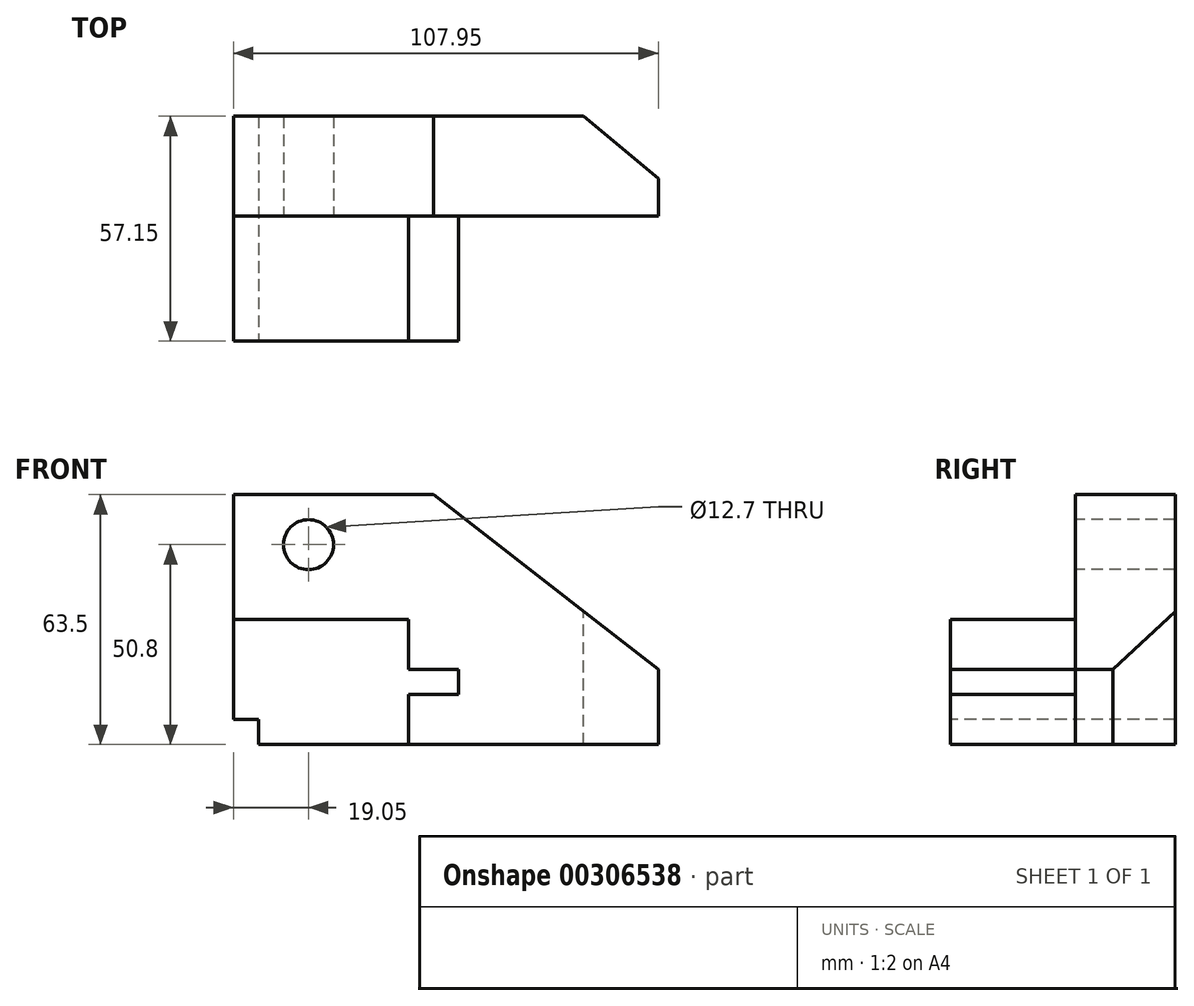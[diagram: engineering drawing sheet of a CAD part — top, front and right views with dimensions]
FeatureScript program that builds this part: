
annotation { "Feature Type Name" : "Feature", "Feature Type Description" : "" }
export const myFeature = defineFeature(function(context is Context, id is Id, definition is map)
    precondition{}
    {
        {
            var Q0;
            Q0=qCreatedBy(makeId("Front.planeOp"),FACE);
            var sketch = newSketch(context, id + "F0", { "sketchPlane" : qUnion([Q0])});
            skLineSegment(sketch, "E0", {"start": v(0, 0) * mm, "end": v(0, 63.5) * mm});
            skLineSegment(sketch, "E1", {"start": v(0, 63.5) * mm, "end": v(107.95, 63.5) * mm});
            skLineSegment(sketch, "E2", {"start": v(107.95, 63.5) * mm, "end": v(107.95, 0) * mm});
            skLineSegment(sketch, "E3", {"start": v(107.95, 0) * mm, "end": v(0, 0) * mm});
            skSolve(sketch);
        }
        {
            var Q0;
            Q0 = qSketchRegion(id + "F0", true);
            extrude(context, id + "F1", {"entities" : qUnion([Q0]), "depth" : 57.15 * mm});
        }
        {
            var Q0;
            Q0=makeQuery(id+"F1.opExtrude","SWEPT_FACE",FACE,{"disambiguationData":[OSD([sQuery(id+"F0.wireOp",EDGE,"E1")])]});
            var sketch = newSketch(context, id + "F2", { "sketchPlane" : qUnion([Q0])});
            skLineSegment(sketch, "E4", {"start": v(0, -57.15) * mm, "end": v(0, -25.4) * mm});
            skLineSegment(sketch, "E5", {"start": v(0, -25.4) * mm, "end": v(107.95, -25.4) * mm});
            skLineSegment(sketch, "E6", {"start": v(107.95, -25.4) * mm, "end": v(107.95, -57.15) * mm});
            skLineSegment(sketch, "E7", {"start": v(107.95, -57.15) * mm, "end": v(0, -57.15) * mm});
            skSolve(sketch);
        }
        {
            var Q0;
            Q0 = qSketchRegion(id + "F2", true);
            extrude(context, id + "F3", {"entities" : qUnion([Q0]), "operationType" : NewBodyOperationType.REMOVE, "oppositeDirection" : true, "depth" : 31.75 * mm});
        }
        {
            var Q0;
            Q0=makeQuery(id+"F1.opExtrude","CAP_FACE",FACE,{"disambiguationData":[OSD([sQuery(id+"F0.wireOp",EDGE,"E0"),sQuery(id+"F0.wireOp",EDGE,"E1"),sQuery(id+"F0.wireOp",EDGE,"E2"),sQuery(id+"F0.wireOp",EDGE,"E3")])],"isStart":false});
            var sketch = newSketch(context, id + "F4", { "sketchPlane" : qUnion([Q0])});
            skLineSegment(sketch, "E8", {"start": v(0, 31.75) * mm, "end": v(44.45, 31.75) * mm});
            skLineSegment(sketch, "E9", {"start": v(44.45, 31.75) * mm, "end": v(44.45, 19.05) * mm});
            skLineSegment(sketch, "E10", {"start": v(44.45, 19.05) * mm, "end": v(57.15, 19.05) * mm});
            skLineSegment(sketch, "E11", {"start": v(57.15, 19.05) * mm, "end": v(57.15, 12.7) * mm});
            skLineSegment(sketch, "E12", {"start": v(57.15, 12.7) * mm, "end": v(44.45, 12.7) * mm});
            skLineSegment(sketch, "E13", {"start": v(44.45, 12.7) * mm, "end": v(44.45, 0) * mm});
            skLineSegment(sketch, "E14", {"start": v(44.45, 0) * mm, "end": v(0, 0) * mm});
            skLineSegment(sketch, "E15", {"start": v(0, 0) * mm, "end": v(0, 31.75) * mm});
            skSolve(sketch);
        }
        {
            var Q0;
            {var subQ0=sQuery(id+"F4.wireOp",EDGE,"E9");Q0=makeQuery(id+"F4.imprint","IMPRINT",FACE,{"disambiguationData":[TD([[makeQuery(id+"F4.imprint","IMPRINT",EDGE,{"derivedFrom":subQ0}),1.0]])]});}
            extrude(context, id + "F5", {"entities" : qUnion([Q0]), "operationType" : NewBodyOperationType.REMOVE, "oppositeDirection" : true, "depth" : 31.75 * mm});
        }
        {
            var Q0;
            Q0=makeQuery(id+"F3.boolean.opBoolean","COPY",FACE,{"derivedFrom":makeQuery(id+"F3.opExtrude","SWEPT_FACE",FACE,{"disambiguationData":[OSD([sQuery(id+"F2.wireOp",EDGE,"E5")])]})});
            var sketch = newSketch(context, id + "F6", { "sketchPlane" : qUnion([Q0])});
            skLineSegment(sketch, "E16", {"start": v(50.8, 63.5) * mm, "end": v(107.95, 19.05) * mm});
            skLineSegment(sketch, "E17", {"start": v(50.8, 63.5) * mm, "end": v(107.95, 63.5) * mm});
            skLineSegment(sketch, "E18", {"start": v(107.95, 63.5) * mm, "end": v(107.95, 19.05) * mm});
            skSolve(sketch);
        }
        {
            var Q0;
            Q0 = qSketchRegion(id + "F6", true);
            extrude(context, id + "F7", {"entities" : qUnion([Q0]), "operationType" : NewBodyOperationType.REMOVE, "endBound" : BoundingType.THROUGH_ALL, "oppositeDirection" : true, "depth" : 25.4 * mm});
        }
        {
            var Q0;
            Q0=makeQuery(id+"F1.opExtrude","CAP_FACE",FACE,{"disambiguationData":[OSD([sQuery(id+"F0.wireOp",EDGE,"E0"),sQuery(id+"F0.wireOp",EDGE,"E1"),sQuery(id+"F0.wireOp",EDGE,"E2"),sQuery(id+"F0.wireOp",EDGE,"E3")])],"isStart":false});
            var sketch = newSketch(context, id + "F8", { "sketchPlane" : qUnion([Q0])});
            skLineSegment(sketch, "E19", {"start": v(0, 0) * mm, "end": v(0, 6.35) * mm});
            skLineSegment(sketch, "E20", {"start": v(0, 6.35) * mm, "end": v(6.35, 6.35) * mm});
            skLineSegment(sketch, "E21", {"start": v(6.35, 6.35) * mm, "end": v(6.35, 0) * mm});
            skLineSegment(sketch, "E22", {"start": v(6.35, 0) * mm, "end": v(0, 0) * mm});
            skSolve(sketch);
        }
        {
            var Q0;
            Q0 = qSketchRegion(id + "F8", true);
            extrude(context, id + "F9", {"entities" : qUnion([Q0]), "operationType" : NewBodyOperationType.REMOVE, "endBound" : BoundingType.THROUGH_ALL, "oppositeDirection" : true, "depth" : 25.4 * mm});
        }
        {
            var Q0;
            Q0=makeQuery(id+"F1.opExtrude","SWEPT_FACE",FACE,{"disambiguationData":[OSD([sQuery(id+"F0.wireOp",EDGE,"E1")])]});
            cPlane(context, id + "F10", {"entities" : qUnion([Q0]), "cplaneType" : CPlaneType.OFFSET, "offset" : 25.4 * mm, "width" : 152.4 * mm, "height" : 152.4 * mm});
        }
        {
            var Q0;
            Q0=qCreatedBy(id+"F10.planeOp",FACE);
            var sketch = newSketch(context, id + "F11", { "sketchPlane" : qUnion([Q0])});
            skLineSegment(sketch, "E23", {"start": v(88.9, 0) * mm, "end": v(107.95, -15.88) * mm});
            skLineSegment(sketch, "E24", {"start": v(107.95, -15.88) * mm, "end": v(107.95, 0) * mm});
            skLineSegment(sketch, "E25", {"start": v(107.95, 0) * mm, "end": v(88.9, 0) * mm});
            skSolve(sketch);
        }
        {
            var Q0;
            Q0 = qSketchRegion(id + "F11", true);
            extrude(context, id + "F12", {"entities" : qUnion([Q0]), "operationType" : NewBodyOperationType.REMOVE, "endBound" : BoundingType.THROUGH_ALL, "oppositeDirection" : true, "depth" : 25.4 * mm});
        }
        {
            var Q0;
            Q0=makeQuery(id+"F3.boolean.opBoolean","COPY",FACE,{"derivedFrom":makeQuery(id+"F3.opExtrude","SWEPT_FACE",FACE,{"disambiguationData":[OSD([sQuery(id+"F2.wireOp",EDGE,"E5")])]})});
            var sketch = newSketch(context, id + "F13", { "sketchPlane" : qUnion([Q0])});
            skCircle(sketch, "E26", {"center": v(19.05, 50.8) * mm, "radius": 6.35 * mm});
            skSolve(sketch);
        }
        {
            var Q0;
            Q0 = qSketchRegion(id + "F13", true);
            extrude(context, id + "F14", {"entities" : qUnion([Q0]), "operationType" : NewBodyOperationType.REMOVE, "endBound" : BoundingType.THROUGH_ALL, "oppositeDirection" : true, "depth" : 25.4 * mm});
        }
    });
